# Revit family: Thorn COLLEGE 2
name_source: partatom
category: Lighting Fixtures
units: mm (PartAtom-declared; Revit-internal decimal feet)

## family parameters
Cut with Voids When Loaded = No
Host = Face
Light Source = Yes
Maintain Annotation Orientation = No
Part Type = Normal
Room Calculation Point = Yes
Round Connector Dimension = Use Diameter
Shared = No

## types (10) — shared parameters
Assembly Code = Pr_70_60_48_45
Besa Mounted = No
Ceiling Mounted = No
Color Filter = 16777215
Contus Track Mounted = No
Description = Surface / Suspended LED Luminaire
Dimming Lamp Color Temperature Shift = <None>
Emit Shape Visible in Rendering = No
Emit from Rectangle Width = 190 mm
Luminaire Height = 82.32 mm  [stored 0.270079 ft]
Luminaire Width = 195.32 mm  [stored 0.640814 ft]
Manufacturer = Thorn Lighting
Power Factor = 0.95
SELECT HOUSING TYPE = SELECT HOUSING TYPE
SELECT MOUNTING OPTION = SELECT MOUNTING OPTION
Suspended = Yes
Tilt Angle = -90.00°
Type Image = COLLEGE 2.jpg
URL = https://www.thornlighting.com
Visibility Besa = No
Visibility Contus = No
Visibility Suspension = Yes
zero-valued in all types: Default Elevation

## per-type parameters (varying)
| type | Apparent Load | Emit from Rectangle Length | Housing L1200 | Housing L1500 | Luminaire Length | Model | Photometric Web File | Suspension Cord Distance |
| COLLEGE2 3000-840 HF L1200 | 25 VA | 1166.5 mm  [stored 3.8271 ft] | Yes | No | 1242 mm  [stored 4.0748 ft] | 96637268 | 96637268_(STD).IES | 1125 mm |
| COLLEGE2 3000-840 HF L1500 | 23 VA | 1466.5 mm  [stored 4.81135 ft] | No | Yes | 1542 mm  [stored 5.05906 ft] | 96637270 | 96637270_(STD).IES | 1425 mm  [stored 4.6752 ft] |
| COLLEGE2 4300-840 HF L1200 | 32 VA | 1166.5 mm  [stored 3.8271 ft] | Yes | No | 1242 mm  [stored 4.0748 ft] | 96637269 | 96637269_(STD).IES | 1125 mm |
| COLLEGE2 4600-840 HF L1500 | 31 VA | 1466.5 mm  [stored 4.81135 ft] | No | Yes | 1542 mm  [stored 5.05906 ft] | 96637271 | 96637271_(STD).IES | 1425 mm  [stored 4.6752 ft] |
| COLLEGE2 6500-840 HF L1500 | 47 VA | 1466.5 mm  [stored 4.81135 ft] | No | Yes | 1542 mm  [stored 5.05906 ft] | 96637272 | 96637272_(STD).IES | 1425 mm  [stored 4.6752 ft] |
| COLLEGE2 3000-840 HFIX L1200 | 25 VA | 1166.5 mm  [stored 3.8271 ft] | Yes | No | 1242 mm  [stored 4.0748 ft] | 96800065 | 96800065_(STD).IES | 1125 mm |
| COLLEGE2 3000-840 HFIX L1500 | 24 VA | 1466.5 mm  [stored 4.81135 ft] | No | Yes | 1542 mm  [stored 5.05906 ft] | 96800067 | 96800067_(STD).IES | 1425 mm  [stored 4.6752 ft] |
| COLLEGE2 4300-840 HFIX L1200 | 32 VA | 1166.5 mm  [stored 3.8271 ft] | Yes | No | 1242 mm  [stored 4.0748 ft] | 96800066 | 96800066_(STD).IES | 1125 mm |
| COLLEGE2 4600-840 HFIX L1500 | 31 VA | 1466.5 mm  [stored 4.81135 ft] | No | Yes | 1542 mm  [stored 5.05906 ft] | 96800068 | 96800068_(STD).IES | 1425 mm  [stored 4.6752 ft] |
| COLLEGE2 6500-840 HFIX L1500 | 48 VA | 1466.5 mm  [stored 4.81135 ft] | No | Yes | 1542 mm  [stored 5.05906 ft] | 96800069 | 96637272_(STD).IES | 1425 mm  [stored 4.6752 ft] |

note: [stored X ft] marks values corroborated as IEEE doubles in the binary element streams (Revit-internal decimal feet)

## geometry (parser evidence)
native form markers: Sweep x7
no freeform markers — native parametric forms only
